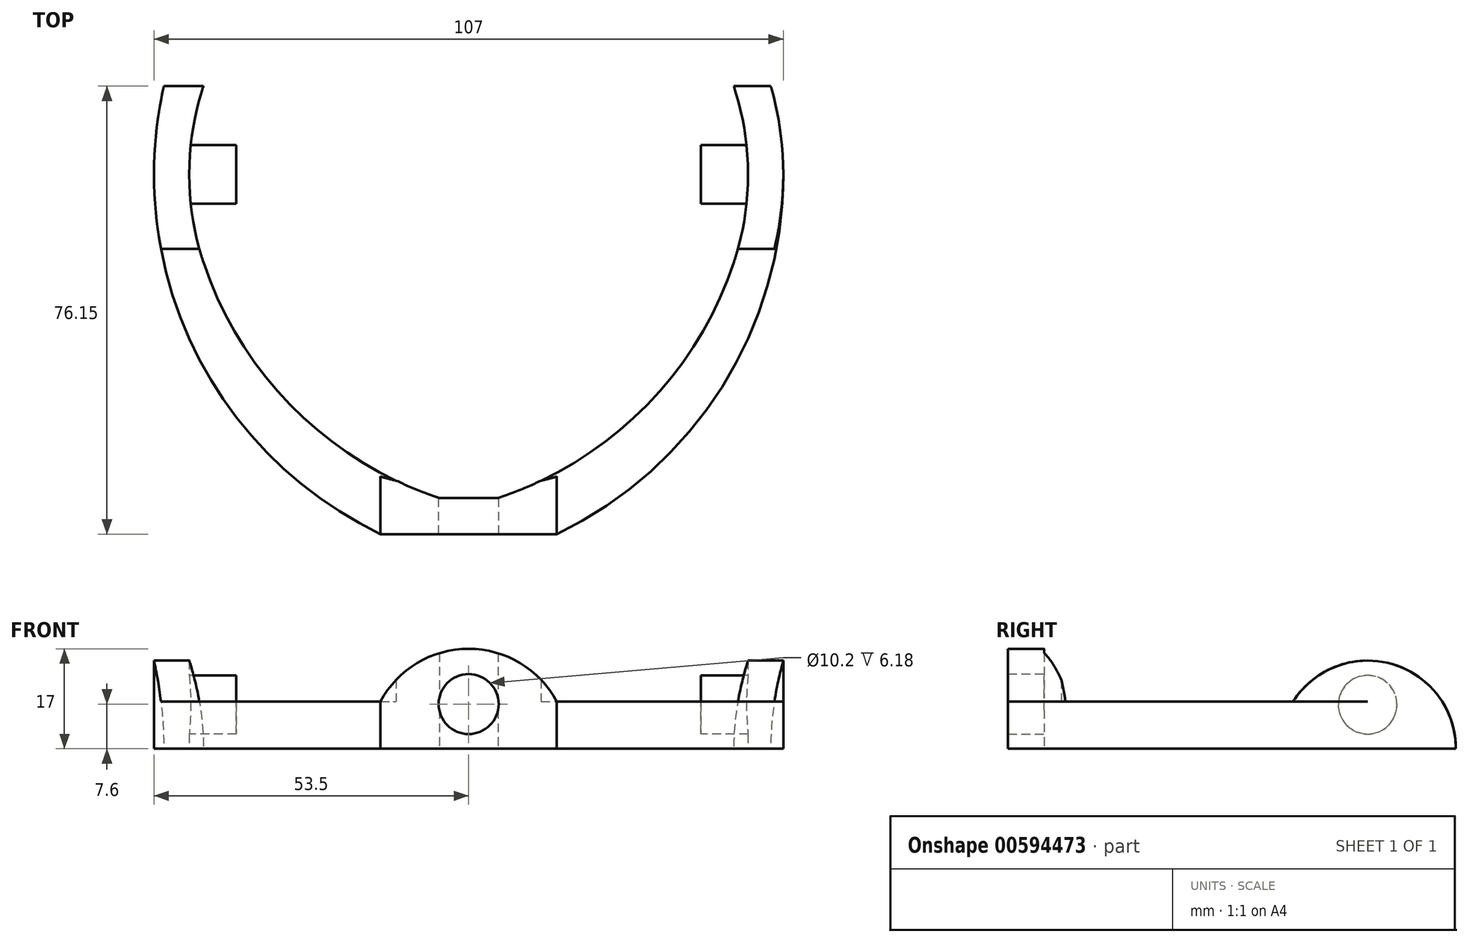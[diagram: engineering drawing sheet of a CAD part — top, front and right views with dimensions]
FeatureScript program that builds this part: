
annotation { "Feature Type Name" : "Feature", "Feature Type Description" : "" }
export const myFeature = defineFeature(function(context is Context, id is Id, definition is map)
    precondition{}
    {
        {
            var Q0;
            Q0=qCreatedBy(makeId("Top.planeOp"),FACE);
            var sketch = newSketch(context, id + "F0", { "sketchPlane" : qUnion([Q0])});
            skCircle(sketch, "E0", {"center": v(0, 0) * mm, "radius": 46 * mm});
            skCircle(sketch, "E1", {"center": v(0, 0) * mm, "radius": 40 * mm});
            skSolve(sketch);
        }
        {
            var Q0;
            Q0=qCreatedBy(makeId("Top.planeOp"),FACE);
            var sketch = newSketch(context, id + "F1", { "sketchPlane" : qUnion([Q0])});
            skArc(sketch, "E2.0", {"start": v(-45.07, 15) * mm, "mid": v(-47.5, 0) * mm, "end": v(-45.07, -15) * mm});
            skArc(sketch, "E3.0", {"start": v(-49.94, 19.18) * mm, "mid": v(-52.6, 9.75) * mm, "end": v(-53.5, 0) * mm});
            skLineSegment(sketch, "E4", {"start": v(0, 0) * mm, "end": v(0, -15) * mm, "construction": true});
            skLineSegment(sketch, "E5", {"start": v(-51.82, -15) * mm, "end": v(51.82, -15) * mm, "construction": true});
            skLineSegment(sketch, "E6", {"start": v(0, -55) * mm, "end": v(0, -65) * mm, "construction": true});
            skLineSegment(sketch, "E7", {"start": v(0, -65) * mm, "end": v(-5, -65) * mm});
            skLineSegment(sketch, "E8", {"start": v(0, -65) * mm, "end": v(5, -65) * mm});
            skArc(sketch, "E9", {"start": v(-53.5, 0) * mm, "mid": v(-53.08, -7.55) * mm, "end": v(-51.82, -15) * mm});
            skArc(sketch, "E10", {"start": v(5, -65) * mm, "mid": v(35.19, -46.35) * mm, "end": v(51.82, -15) * mm});
            skArc(sketch, "E11.trimOffspring", {"start": v(53.5, 0) * mm, "mid": v(52.6, 9.75) * mm, "end": v(49.94, 19.18) * mm});
            skLineSegment(sketch, "E12", {"start": v(-45.07, 15) * mm, "end": v(-49.94, 19.18) * mm});
            skLineSegment(sketch, "E13", {"start": v(45.07, 15) * mm, "end": v(49.94, 19.18) * mm});
            skLineSegment(sketch, "E14", {"start": v(-45.07, 15) * mm, "end": v(45.07, 15) * mm, "construction": true});
            skLineSegment(sketch, "E15", {"start": v(0, 0) * mm, "end": v(0, 15) * mm, "construction": true});
            skArc(sketch, "E16", {"start": v(-45.07, -15) * mm, "mid": v(0, -47.5) * mm, "end": v(45.07, -15) * mm, "construction": true});
            skArc(sketch, "E17", {"start": v(45.07, -15) * mm, "mid": v(47.5, 0) * mm, "end": v(45.07, 15) * mm});
            skArc(sketch, "E18", {"start": v(-51.82, -15) * mm, "mid": v(-35.19, -46.35) * mm, "end": v(-5, -65) * mm});
            skArc(sketch, "E19", {"start": v(51.82, -15) * mm, "mid": v(53.08, -7.55) * mm, "end": v(53.5, 0) * mm});
            skLineSegment(sketch, "E20", {"start": v(-5, -55) * mm, "end": v(0, -55) * mm});
            skLineSegment(sketch, "E21", {"start": v(0, -55) * mm, "end": v(5, -55) * mm});
            skArc(sketch, "E22", {"start": v(-45.07, -15) * mm, "mid": v(-29.77, -39.74) * mm, "end": v(-5, -55) * mm});
            skArc(sketch, "E23", {"start": v(5, -55) * mm, "mid": v(29.77, -39.74) * mm, "end": v(45.07, -15) * mm});
            skSolve(sketch);
        }
        {
            var Q0;
            Q0=qSketchRegion(id+"F1",true);
            extrude(context, id + "F2", {"entities" : qUnion([Q0]), "depth" : 8 * mm});
        }
        {
            var Q0;
            Q0=qCreatedBy(makeId("Right.planeOp"),FACE);
            var sketch = newSketch(context, id + "F3", { "sketchPlane" : qUnion([Q0])});
            skArc(sketch, "E24", {"start": v(15, 0) * mm, "mid": v(0, 15) * mm, "end": v(-15, 0) * mm});
            skLineSegment(sketch, "E25", {"start": v(-15, 0) * mm, "end": v(15, 0) * mm});
            skSolve(sketch);
        }
        {
            var Q0;
            Q0=qSketchRegion(id+"F3",true);
            var Q1;
            Q1=makeQuery(id+"F2.opExtrude","SWEPT_FACE",FACE,{"disambiguationData":[OSD([sQuery(id+"F1.wireOp",EDGE,"E9")])]});
            var Q2;
            Q2=makeQuery(id+"F2.opExtrude","SWEPT_FACE",FACE,{"disambiguationData":[OSD([sQuery(id+"F1.wireOp",EDGE,"E2.0")])]});
            extrude(context, id + "F4", {"entities" : qUnion([Q0]), "operationType" : NewBodyOperationType.ADD, "endBound" : BoundingType.UP_TO_SURFACE, "oppositeDirection" : true, "endBoundEntityFace" : qUnion([Q1]), "depth" : 25 * mm, "hasSecondDirection" : true, "secondDirectionBound" : SecondDirectionBoundingType.UP_TO_SURFACE, "secondDirectionOppositeDirection" : true, "secondDirectionBoundEntityFace" : qUnion([Q2]), "secondDirectionDepth" : 25 * mm});
        }
        {
            var Q0;
            Q0=qCreatedBy(makeId("Right.planeOp"),FACE);
            var sketch = newSketch(context, id + "F5", { "sketchPlane" : qUnion([Q0])});
            skArc(sketch, "E26", {"start": v(15, 0) * mm, "mid": v(0, 15) * mm, "end": v(-15, 0) * mm});
            skLineSegment(sketch, "E27", {"start": v(-15, 0) * mm, "end": v(15, 0) * mm});
            skSolve(sketch);
        }
        {
            var Q0;
            Q0=qSketchRegion(id+"F5",true);
            var Q1;
            Q1=makeQuery(id+"F2.opExtrude","SWEPT_FACE",FACE,{"disambiguationData":[OSD([sQuery(id+"F1.wireOp",EDGE,"E11.trimOffspring")])]});
            var Q2;
            Q2=makeQuery(id+"F4.boolean.opBoolean","MERGE",FACE,{"derivedFrom":[makeQuery(id+"F2.opExtrude","SWEPT_FACE",FACE,{"disambiguationData":[OSD([sQuery(id+"F1.wireOp",EDGE,"E2.0")])]}),makeQuery(id+"F4.opExtrude","CAP_FACE",FACE,{"disambiguationData":[OSD([sQuery(id+"F3.wireOp",EDGE,"E24"),sQuery(id+"F3.wireOp",EDGE,"E25")]),OD(1.0)],"isStart":false})]});
            extrude(context, id + "F6", {"entities" : qUnion([Q0]), "operationType" : NewBodyOperationType.ADD, "endBound" : BoundingType.UP_TO_SURFACE, "endBoundEntityFace" : qUnion([Q1]), "depth" : 25 * mm, "hasSecondDirection" : true, "secondDirectionBound" : SecondDirectionBoundingType.UP_TO_SURFACE, "secondDirectionOppositeDirection" : false, "secondDirectionBoundEntityFace" : qUnion([Q2]), "secondDirectionDepth" : 25 * mm});
        }
        {
            var Q0;
            Q0=qCreatedBy(makeId("Right.planeOp"),FACE);
            var sketch = newSketch(context, id + "F7", { "sketchPlane" : qUnion([Q0])});
            skArc(sketch, "E28", {"start": v(15, 0) * mm, "mid": v(10.6, 10.6) * mm, "end": v(0, 15) * mm});
            skLineSegment(sketch, "E29", {"start": v(0, 15) * mm, "end": v(20.32, 15) * mm});
            skLineSegment(sketch, "E30", {"start": v(20.32, 15) * mm, "end": v(20.32, 0) * mm});
            skLineSegment(sketch, "E31", {"start": v(20.32, 0) * mm, "end": v(15, 0) * mm});
            skSolve(sketch);
        }
        {
            var Q0;
            Q0=qSketchRegion(id+"F7",true);
            extrude(context, id + "F8", {"entities" : qUnion([Q0]), "operationType" : NewBodyOperationType.REMOVE, "endBound" : BoundingType.THROUGH_ALL, "oppositeDirection" : true, "depth" : 25 * mm, "hasSecondDirection" : true, "secondDirectionBound" : SecondDirectionBoundingType.THROUGH_ALL, "secondDirectionOppositeDirection" : false, "secondDirectionDepth" : 25 * mm});
        }
        {
            var Q0;
            Q0=qCreatedBy(makeId("Right.planeOp"),FACE);
            var sketch = newSketch(context, id + "F9", { "sketchPlane" : qUnion([Q0])});
            skCircle(sketch, "E32", {"center": v(0, 7.5) * mm, "radius": 5 * mm});
            skSolve(sketch);
        }
        {
            var Q0;
            Q0=qSketchRegion(id+"F9",true);
            var Q1;
            Q1=makeQuery(id+"F6.boolean.opBoolean","MERGE",FACE,{"derivedFrom":[makeQuery(id+"F4.boolean.opBoolean","MERGE",FACE,{"derivedFrom":[makeQuery(id+"F2.opExtrude","SWEPT_FACE",FACE,{"disambiguationData":[OSD([sQuery(id+"F1.wireOp",EDGE,"E2.0")])]}),makeQuery(id+"F4.opExtrude","CAP_FACE",FACE,{"disambiguationData":[OSD([sQuery(id+"F3.wireOp",EDGE,"E24"),sQuery(id+"F3.wireOp",EDGE,"E25")]),OD(1.0)],"isStart":false})]}),makeQuery(id+"F6.opExtrude","CAP_FACE",FACE,{"disambiguationData":[OSD([sQuery(id+"F5.wireOp",EDGE,"E26"),sQuery(id+"F5.wireOp",EDGE,"E27")]),OD(0.0)],"isStart":false})]});
            var Q2;
            Q2=makeQuery(id+"F6.boolean.opBoolean","MERGE",FACE,{"derivedFrom":[makeQuery(id+"F4.boolean.opBoolean","MERGE",FACE,{"derivedFrom":[makeQuery(id+"F2.opExtrude","SWEPT_FACE",FACE,{"disambiguationData":[OSD([sQuery(id+"F1.wireOp",EDGE,"E2.0")])]}),makeQuery(id+"F4.opExtrude","CAP_FACE",FACE,{"disambiguationData":[OSD([sQuery(id+"F3.wireOp",EDGE,"E24"),sQuery(id+"F3.wireOp",EDGE,"E25")]),OD(1.0)],"isStart":false})]}),makeQuery(id+"F6.opExtrude","CAP_FACE",FACE,{"disambiguationData":[OSD([sQuery(id+"F5.wireOp",EDGE,"E26"),sQuery(id+"F5.wireOp",EDGE,"E27")]),OD(0.0)],"isStart":false})]});
            extrude(context, id + "F10", {"entities" : qUnion([Q0]), "operationType" : NewBodyOperationType.ADD, "endBound" : BoundingType.UP_TO_SURFACE, "endBoundEntityFace" : qUnion([Q1]), "depth" : 25 * mm, "hasSecondDirection" : true, "secondDirectionBound" : SecondDirectionBoundingType.UP_TO_SURFACE, "secondDirectionOppositeDirection" : true, "secondDirectionBoundEntityFace" : qUnion([Q2]), "secondDirectionDepth" : 25 * mm});
        }
        {
            var Q0;
            Q0=qCreatedBy(makeId("Top.planeOp"),FACE);
            var sketch = newSketch(context, id + "F11", { "sketchPlane" : qUnion([Q0])});
            skLineSegment(sketch, "E33.bottom", {"start": v(39.5, -13.07) * mm, "end": v(-39.5, -13.07) * mm});
            skLineSegment(sketch, "E33.top", {"start": v(39.5, 13.07) * mm, "end": v(-39.5, 13.07) * mm});
            skLineSegment(sketch, "E33.left", {"start": v(39.5, -13.07) * mm, "end": v(39.5, 13.07) * mm});
            skLineSegment(sketch, "E33.right", {"start": v(-39.5, -13.07) * mm, "end": v(-39.5, 13.07) * mm});
            skPoint(sketch, "E33.middle", {"position": v(0, 0) * mm});
            skSolve(sketch);
        }
        {
            var Q0;
            Q0=qSketchRegion(id+"F11",true);
            extrude(context, id + "F12", {"entities" : qUnion([Q0]), "operationType" : NewBodyOperationType.REMOVE, "endBound" : BoundingType.THROUGH_ALL, "depth" : 25 * mm});
        }
        {
            var Q0;
            Q0=qCreatedBy(makeId("Front.planeOp"),FACE);
            var sketch = newSketch(context, id + "F13", { "sketchPlane" : qUnion([Q0])});
            skArc(sketch, "E34", {"start": v(17, 0) * mm, "mid": v(0, 17) * mm, "end": v(-17, 0) * mm});
            skLineSegment(sketch, "E35", {"start": v(-17, 0) * mm, "end": v(17, 0) * mm});
            skSolve(sketch);
        }
        {
            var Q0;
            Q0=qSketchRegion(id+"F13",true);
            var Q1;
            {var subQ0=sQuery(id+"F1.wireOp",EDGE,"E10");var subQ1=sQuery(id+"F3.wireOp",EDGE,"E25");var subQ2=sQuery(id+"F1.wireOp",EDGE,"E9");var subQ3=sQuery(id+"F1.wireOp",EDGE,"E8");var subQ4=sQuery(id+"F1.wireOp",EDGE,"E7");Q1=makeQuery(id+"F16.boolean.opBoolean","SPLIT",FACE,{"disambiguationData":[TD([makeQuery(id+"F2.opExtrude","CAP_FACE",FACE,{"disambiguationData":[OSD([sQuery(id+"F1.wireOp",EDGE,"E2.0"),sQuery(id+"F1.wireOp",EDGE,"E3.0"),subQ4,subQ3,subQ2,subQ0,sQuery(id+"F1.wireOp",EDGE,"E11.trimOffspring"),sQuery(id+"F1.wireOp",EDGE,"E12"),sQuery(id+"F1.wireOp",EDGE,"E13")])],"isStart":true}),makeQuery(id+"F2.opExtrude","SWEPT_FACE",FACE,{"disambiguationData":[OSD([subQ2])]}),makeQuery(id+"F2.opExtrude","SWEPT_FACE",FACE,{"disambiguationData":[OSD([subQ0])]}),makeQuery(id+"F4.opExtrude","SWEPT_FACE",FACE,{"disambiguationData":[OSD([subQ1])]}),makeQuery(id+"F4.opExtrude","CAP_FACE",FACE,{"disambiguationData":[OSD([sQuery(id+"F3.wireOp",EDGE,"E24"),subQ1]),OD(0.0)],"isStart":false}),makeQuery(id+"F16.opExtrude","SWEPT_FACE",FACE,{"disambiguationData":[OSD([sQuery(id+"F15.wireOp",EDGE,"E36")])]})])],"derivedFrom":makeQuery(id+"F2.opExtrude","SWEPT_FACE",FACE,{"disambiguationData":[OSD([subQ4,subQ3])]})});}
            var Q2;
            Q2=makeQuery(id+"F6.boolean.opBoolean","MERGE",FACE,{"derivedFrom":[makeQuery(id+"F4.boolean.opBoolean","MERGE",FACE,{"derivedFrom":[makeQuery(id+"F2.opExtrude","SWEPT_FACE",FACE,{"disambiguationData":[OSD([sQuery(id+"F1.wireOp",EDGE,"E2.0")])]}),makeQuery(id+"F4.opExtrude","CAP_FACE",FACE,{"disambiguationData":[OSD([sQuery(id+"F3.wireOp",EDGE,"E24"),sQuery(id+"F3.wireOp",EDGE,"E25")]),OD(1.0)],"isStart":false})]}),makeQuery(id+"F6.opExtrude","CAP_FACE",FACE,{"disambiguationData":[OSD([sQuery(id+"F5.wireOp",EDGE,"E26"),sQuery(id+"F5.wireOp",EDGE,"E27")]),OD(0.0)],"isStart":false})]});
            extrude(context, id + "F14", {"entities" : qUnion([Q0]), "operationType" : NewBodyOperationType.ADD, "endBound" : BoundingType.UP_TO_SURFACE, "endBoundEntityFace" : qUnion([Q1]), "depth" : 25 * mm, "hasSecondDirection" : true, "secondDirectionBound" : SecondDirectionBoundingType.UP_TO_SURFACE, "secondDirectionOppositeDirection" : false, "secondDirectionBoundEntityFace" : qUnion([Q2]), "secondDirectionDepth" : 25 * mm});
        }
        {
            var Q0;
            Q0=qCreatedBy(makeId("Front.planeOp"),FACE);
            var sketch = newSketch(context, id + "F15", { "sketchPlane" : qUnion([Q0])});
            skCircle(sketch, "E36", {"center": v(0, 7.6) * mm, "radius": 5.1 * mm});
            skSolve(sketch);
        }
        {
            var Q0;
            Q0=qSketchRegion(id+"F15",true);
            extrude(context, id + "F16", {"entities" : qUnion([Q0]), "operationType" : NewBodyOperationType.REMOVE, "endBound" : BoundingType.THROUGH_ALL, "depth" : 25 * mm});
        }
        {
            var Q0;
            Q0=qCreatedBy(makeId("Top.planeOp"),FACE);
            var sketch = newSketch(context, id + "F17", { "sketchPlane" : qUnion([Q0])});
            skArc(sketch, "E37.0", {"start": v(-52.3, -12.69) * mm, "mid": v(-39.42, -41.36) * mm, "end": v(-15, -61.15) * mm});
            skArc(sketch, "E38.0", {"start": v(15, -61.15) * mm, "mid": v(43.07, -36.13) * mm, "end": v(53.5, 0) * mm});
            skLineSegment(sketch, "E39", {"start": v(-52.3, -12.69) * mm, "end": v(-52.3, -67.22) * mm});
            skLineSegment(sketch, "E40", {"start": v(-52.3, -67.22) * mm, "end": v(53.5, -67.22) * mm});
            skLineSegment(sketch, "E41", {"start": v(53.5, -67.22) * mm, "end": v(53.5, 0) * mm});
            skLineSegment(sketch, "E42", {"start": v(-15, -61.15) * mm, "end": v(15, -61.15) * mm});
            skSolve(sketch);
        }
        {
            var Q0;
            Q0=qSketchRegion(id+"F17",true);
            extrude(context, id + "F18", {"entities" : qUnion([Q0]), "operationType" : NewBodyOperationType.REMOVE, "endBound" : BoundingType.THROUGH_ALL, "depth" : 25 * mm});
        }
        {
            var Q0;
            Q0=makeQuery(id+"F1.imprint","IMPRINT",FACE,{"disambiguationData":[TD([[makeQuery(id+"F1.imprint","IMPRINT",EDGE,{"derivedFrom":sQuery(id+"F1.wireOp",EDGE,"E2.0")}),-1.0]])]});
            var sketch = newSketch(context, id + "F19", { "sketchPlane" : qUnion([Q0])});
            skArc(sketch, "E43.0", {"start": v(-45.07, -15) * mm, "mid": v(-29.77, -39.74) * mm, "end": v(-5, -55) * mm});
            skLineSegment(sketch, "E43.1", {"start": v(-5, -55) * mm, "end": v(0, -55) * mm});
            skLineSegment(sketch, "E43.2", {"start": v(0, -55) * mm, "end": v(5, -55) * mm});
            skArc(sketch, "E43.3", {"start": v(5, -55) * mm, "mid": v(29.77, -39.74) * mm, "end": v(45.07, -15) * mm});
            skLineSegment(sketch, "E44", {"start": v(-45.07, -15) * mm, "end": v(45.07, -15) * mm});
            skSolve(sketch);
        }
        {
            var Q0;
            Q0=qSketchRegion(id+"F19",true);
            extrude(context, id + "F20", {"entities" : qUnion([Q0]), "operationType" : NewBodyOperationType.REMOVE, "endBound" : BoundingType.THROUGH_ALL, "depth" : 25 * mm});
        }
    });
